# Revit family: BIM_Model_Piranha_50_S17_2W_rfa
name_source: partatom
category: Mechanical Equipment
revit_build: Autodesk Revit 2018 (Build: 20170223_1515(x64)
units: mm (PartAtom-declared; Revit-internal decimal feet)

## family parameters
Always vertical = Yes
Cut with Voids When Loaded = No
Part Type = Normal
Room Calculation Point = No
Round Connector Dimension = Use Radius
Shared = No
Work Plane-Based = No

## types (1)
- Piranha S17/2W
    Cable Length (m) = 10m
    Cable Size = 4G1.5
    Capacity(m3/hr) = 30 m³
    Description = Submersible pumps for problem-free pumping of sewage
containing faecal matter in pipe lines from 1¼” (DN 32).
    Fasteners = Stainless steel 1.4401 (AISI 316)
    Head(m) = 75 mm
    Impeller = Cast Iron EN-GJL-250
    Manufacturer = Sulzer
    Model = Submersible Grinder Pump Type ABS Piranha S17/2W
    Motor Housing = Cast Iron EN-GJL-250
    Motor Power (kW) = P1=2.36 P2=1.65
    Product Specification Link = https://www.sulzer.com
    Rated Current (A) = 10.60
    Rated Voltage (V) = 220-240 1~
    Rotor Shaft = Stainless steel 1.4021 (AISI 420)
    Speed (r/min) = 2900
    Volute = Cast Iron EN-GJL-250

## geometry (parser evidence)
native form markers: Sweep x3
no freeform markers — native parametric forms only
